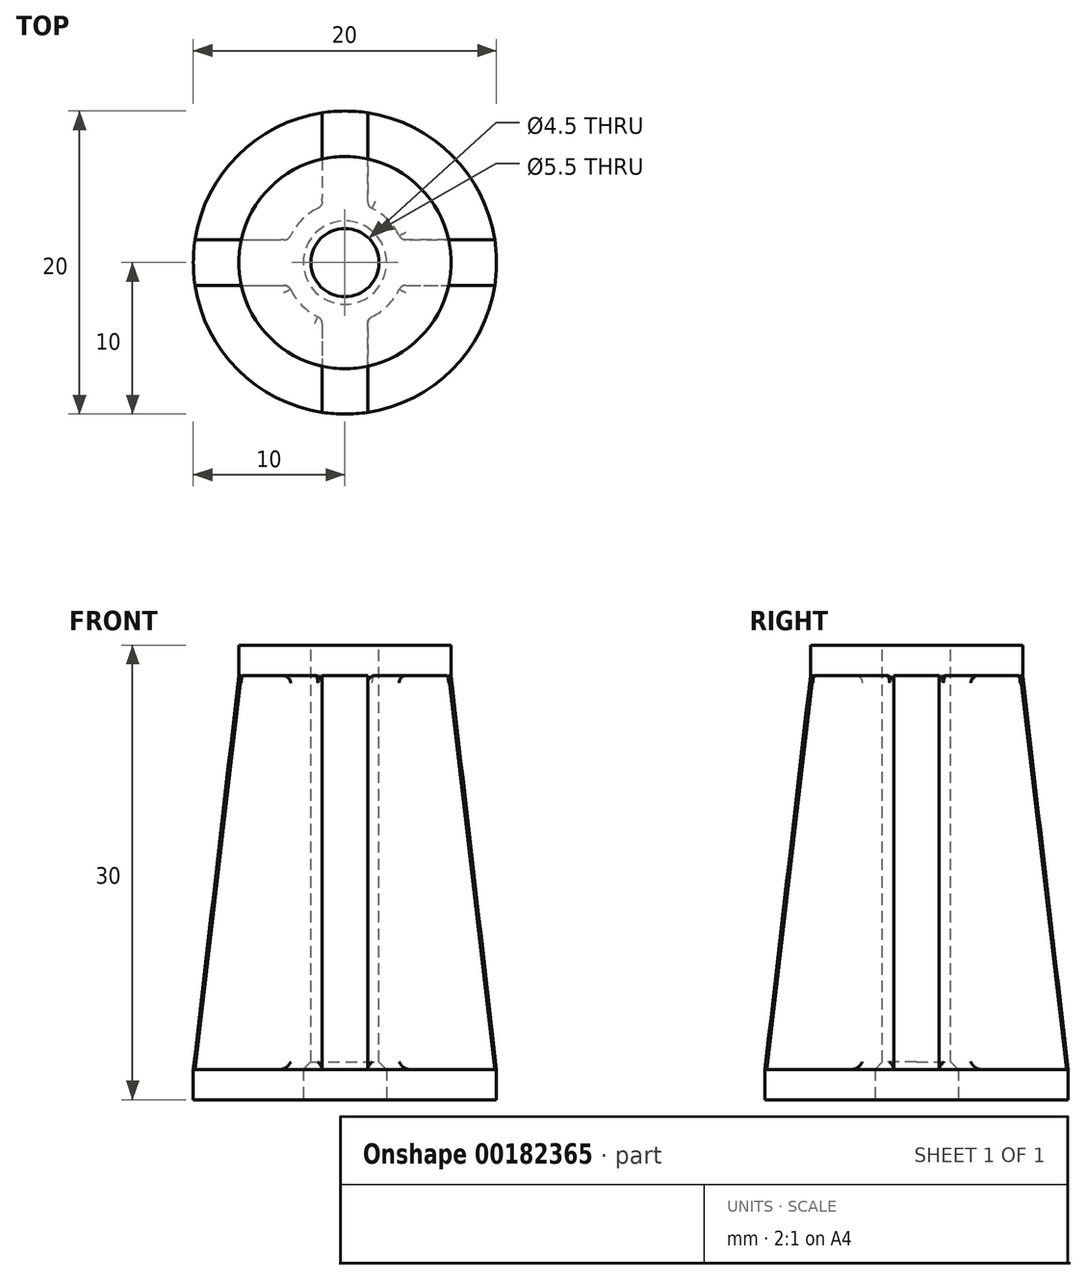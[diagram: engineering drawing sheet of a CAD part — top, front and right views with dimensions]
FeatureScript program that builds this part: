
annotation { "Feature Type Name" : "Feature", "Feature Type Description" : "" }
export const myFeature = defineFeature(function(context is Context, id is Id, definition is map)
    precondition{}
    {
        {
            var Q0;
            Q0=qCreatedBy(makeId("Top.planeOp"),FACE);
            cPlane(context, id + "F0", {"entities" : qUnion([Q0]), "cplaneType" : CPlaneType.OFFSET, "offset" : 28 * mm, "width" : 150 * mm, "height" : 150 * mm});
        }
        {
            var Q0;
            Q0=qCreatedBy(makeId("Top.planeOp"),FACE);
            var sketch = newSketch(context, id + "F1", { "sketchPlane" : qUnion([Q0])});
            skCircle(sketch, "E0", {"center": v(0, 0) * mm, "radius": 10 * mm});
            skSolve(sketch);
        }
        {
            var Q0;
            Q0 = qSketchRegion(id + "F1", true);
            extrude(context, id + "F2", {"entities" : qUnion([Q0]), "depth" : 2 * mm, "offsetDistance" : 25 * mm});
        }
        {
            var Q0;
            Q0=makeQuery(id+"F2.opExtrude","CAP_FACE",FACE,{"disambiguationData":[OSD([sQuery(id+"F1.wireOp",EDGE,"0cac81a4-8bcc-4151-b26c-005e9ad481a4"),sQuery(id+"F1.wireOp",EDGE,"E0")])],"isStart":false});
            var sketch = newSketch(context, id + "F3", { "sketchPlane" : qUnion([Q0])});
            skLineSegment(sketch, "E1", {"start": v(-7.41, 0) * mm, "end": v(8.18, 0) * mm, "construction": true});
            skLineSegment(sketch, "E2", {"start": v(0, 6.98) * mm, "end": v(0, -7.13) * mm, "construction": true});
            skArc(sketch, "E3.0", {"start": v(-1.5, -9.89) * mm, "mid": v(0, -10) * mm, "end": v(1.5, -9.89) * mm});
            skLineSegment(sketch, "E4.0", {"start": v(-9.89, -1.5) * mm, "end": v(-3.7, -1.5) * mm});
            skLineSegment(sketch, "E5.0", {"start": v(-9.89, 1.5) * mm, "end": v(-3.7, 1.5) * mm});
            skLineSegment(sketch, "E6.0", {"start": v(-1.5, 9.89) * mm, "end": v(-1.5, 3.7) * mm});
            skLineSegment(sketch, "E7.0", {"start": v(1.5, 9.89) * mm, "end": v(1.5, 3.7) * mm});
            skArc(sketch, "E8.trimOffspring", {"start": v(9.89, -1.5) * mm, "mid": v(10, 0) * mm, "end": v(9.89, 1.5) * mm});
            skArc(sketch, "E9.trimOffspring", {"start": v(1.5, 9.89) * mm, "mid": v(0, 10) * mm, "end": v(-1.5, 9.89) * mm});
            skArc(sketch, "E10.trimOffspring", {"start": v(-9.89, 1.5) * mm, "mid": v(-10, 0) * mm, "end": v(-9.89, -1.5) * mm});
            skLineSegment(sketch, "E11.trimOffspring", {"start": v(3.7, -1.5) * mm, "end": v(9.89, -1.5) * mm});
            skLineSegment(sketch, "E12.trimOffspring", {"start": v(-1.5, -3.7) * mm, "end": v(-1.5, -9.89) * mm});
            skLineSegment(sketch, "E13.trimOffspring", {"start": v(1.5, -3.7) * mm, "end": v(1.5, -9.89) * mm});
            skArc(sketch, "E14", {"start": v(-3.7, -1.5) * mm, "mid": v(-2.83, -2.83) * mm, "end": v(-1.5, -3.7) * mm});
            skArc(sketch, "E15.trimOffspring", {"start": v(-1.5, 3.7) * mm, "mid": v(-2.83, 2.83) * mm, "end": v(-3.7, 1.5) * mm});
            skLineSegment(sketch, "E16.trimOffspring", {"start": v(3.7, 1.5) * mm, "end": v(9.89, 1.5) * mm});
            skArc(sketch, "E17.trimOffspring", {"start": v(3.7, 1.5) * mm, "mid": v(2.83, 2.83) * mm, "end": v(1.5, 3.7) * mm});
            skArc(sketch, "E18.trimOffspring", {"start": v(1.5, -3.7) * mm, "mid": v(2.83, -2.83) * mm, "end": v(3.7, -1.5) * mm});
            skSolve(sketch);
        }
        {
            var Q0;
            Q0=qCreatedBy(id+"F0.planeOp",FACE);
            var sketch = newSketch(context, id + "F4", { "sketchPlane" : qUnion([Q0])});
            skArc(sketch, "E19", {"start": v(-6.84, 1.5) * mm, "mid": v(-7, 0) * mm, "end": v(-6.84, -1.5) * mm});
            skLineSegment(sketch, "E20.0", {"start": v(1.5, 6.84) * mm, "end": v(1.5, 3.7) * mm});
            skLineSegment(sketch, "E21.0", {"start": v(3.7, 1.5) * mm, "end": v(6.84, 1.5) * mm});
            skLineSegment(sketch, "E22.0", {"start": v(3.7, -1.5) * mm, "end": v(6.84, -1.5) * mm});
            skLineSegment(sketch, "E23.0", {"start": v(1.5, -3.7) * mm, "end": v(1.5, -6.84) * mm});
            skLineSegment(sketch, "E24.0", {"start": v(-1.5, -3.7) * mm, "end": v(-1.5, -6.84) * mm});
            skLineSegment(sketch, "E25.0", {"start": v(-6.84, -1.5) * mm, "end": v(-3.7, -1.5) * mm});
            skLineSegment(sketch, "E26.0", {"start": v(-6.84, 1.5) * mm, "end": v(-3.7, 1.5) * mm});
            skLineSegment(sketch, "E27.0", {"start": v(-1.5, 6.84) * mm, "end": v(-1.5, 3.7) * mm});
            skPoint(sketch, "E28.orphan", {"position": v(1.5, 9.89) * mm});
            skPoint(sketch, "E29.orphan", {"position": v(-1.5, 9.89) * mm});
            skPoint(sketch, "E30.orphan", {"position": v(-9.89, 1.5) * mm});
            skPoint(sketch, "E31.orphan", {"position": v(-9.89, -1.5) * mm});
            skArc(sketch, "E32.trimOffspring", {"start": v(-1.5, -6.84) * mm, "mid": v(0, -7) * mm, "end": v(1.5, -6.84) * mm});
            skArc(sketch, "E33.trimOffspring", {"start": v(6.84, -1.5) * mm, "mid": v(7, 0) * mm, "end": v(6.84, 1.5) * mm});
            skPoint(sketch, "E34.orphan", {"position": v(1.5, -9.89) * mm});
            skPoint(sketch, "E35.orphan", {"position": v(-1.5, -9.89) * mm});
            skPoint(sketch, "E36.orphan", {"position": v(9.89, -1.5) * mm});
            skPoint(sketch, "E37.orphan", {"position": v(5.92, 1.5) * mm});
            skArc(sketch, "E38.trimOffspring", {"start": v(1.5, 6.84) * mm, "mid": v(0, 7) * mm, "end": v(-1.5, 6.84) * mm});
            skArc(sketch, "E39", {"start": v(-3.7, -1.5) * mm, "mid": v(-2.83, -2.83) * mm, "end": v(-1.5, -3.7) * mm});
            skArc(sketch, "E40.trimOffspring", {"start": v(-1.5, 3.7) * mm, "mid": v(-2.83, 2.83) * mm, "end": v(-3.7, 1.5) * mm});
            skArc(sketch, "E41.trimOffspring", {"start": v(1.5, -3.7) * mm, "mid": v(2.83, -2.83) * mm, "end": v(3.7, -1.5) * mm});
            skArc(sketch, "E42.trimOffspring", {"start": v(3.7, 1.5) * mm, "mid": v(2.83, 2.83) * mm, "end": v(1.5, 3.7) * mm});
            skSolve(sketch);
        }
        {
            var Q1;
            Q1 = qSketchRegion(id + "F3", true);
            var Q2;
            Q2 = qSketchRegion(id + "F4", true);
            loft(context, id + "F5", {"operationType" : NewBodyOperationType.ADD, "sheetProfilesArray" : [{ "sheetProfileEntities" : qUnion([Q1]) }, { "sheetProfileEntities" : qUnion([Q2]) }]});
        }
        {
            var Q0;
            Q0=makeQuery(id+"F5.opLoft","CAP_FACE",FACE,{"disambiguationData":[OSD([makeQuery(id+"F4.imprint","IMPRINT",FACE,{"disambiguationData":[TD([[makeQuery(id+"F4.imprint","IMPRINT",EDGE,{"derivedFrom":sQuery(id+"F4.wireOp",EDGE,"E19")}),1.0]])]})])],"isStart":true});
            var sketch = newSketch(context, id + "F6", { "sketchPlane" : qUnion([Q0])});
            skCircle(sketch, "E43", {"center": v(0, 0) * mm, "radius": 7 * mm});
            skSolve(sketch);
        }
        {
            var Q0;
            Q0 = qSketchRegion(id + "F6", true);
            extrude(context, id + "F7", {"entities" : qUnion([Q0]), "operationType" : NewBodyOperationType.ADD, "depth" : 2 * mm, "offsetDistance" : 25 * mm});
        }
        {
            var Q0;
            Q0=makeQuery(id+"F7.opExtrude","CAP_FACE",FACE,{"disambiguationData":[OSD([sQuery(id+"F6.wireOp",EDGE,"E43")])],"isStart":false});
            var sketch = newSketch(context, id + "F8", { "sketchPlane" : qUnion([Q0])});
            skCircle(sketch, "E44", {"center": v(0, 0) * mm, "radius": 2.25 * mm});
            skSolve(sketch);
        }
        {
            var Q0;
            Q0 = qSketchRegion(id + "F8", true);
            extrude(context, id + "F9", {"entities" : qUnion([Q0]), "operationType" : NewBodyOperationType.REMOVE, "endBound" : BoundingType.THROUGH_ALL, "oppositeDirection" : true, "depth" : 25 * mm, "offsetDistance" : 25 * mm});
        }
        {
            var Q0;
            Q0=makeQuery(id+"F5.opLoft","MID_CAP_EDGE",EDGE,{"disambiguationData":[OSD([sQuery(id+"F3.wireOp",EDGE,"E5.0"),sQuery(id+"F3.wireOp",EDGE,"E6.0"),sQuery(id+"F3.wireOp",EDGE,"E15.trimOffspring")])],"capPos":0.0});
            var Q1;
            Q1=makeQuery(id+"F5.opLoft","SWEPT_EDGE",EDGE,{"disambiguationData":[OSD([sQuery(id+"F3.wireOp",EDGE,"E6.0"),sQuery(id+"F3.wireOp",EDGE,"E15.trimOffspring"),sQuery(id+"F4.wireOp",EDGE,"E27.0"),sQuery(id+"F4.wireOp",EDGE,"E40.trimOffspring")])]});
            var Q2;
            Q2=makeQuery(id+"F5.opLoft","SWEPT_FACE",FACE,{"disambiguationData":[OSD([sQuery(id+"F3.wireOp",EDGE,"E5.0"),sQuery(id+"F3.wireOp",EDGE,"E6.0"),sQuery(id+"F3.wireOp",EDGE,"E15.trimOffspring"),sQuery(id+"F4.wireOp",EDGE,"E26.0"),sQuery(id+"F4.wireOp",EDGE,"E27.0"),sQuery(id+"F4.wireOp",EDGE,"E40.trimOffspring")])]});
            var Q3;
            Q3=makeQuery(id+"F5.opLoft","SWEPT_FACE",FACE,{"disambiguationData":[OSD([sQuery(id+"F3.wireOp",EDGE,"E4.0"),sQuery(id+"F3.wireOp",EDGE,"E12.trimOffspring"),sQuery(id+"F3.wireOp",EDGE,"E14"),sQuery(id+"F4.wireOp",EDGE,"E24.0"),sQuery(id+"F4.wireOp",EDGE,"E25.0"),sQuery(id+"F4.wireOp",EDGE,"E39")])]});
            var Q4;
            Q4=makeQuery(id+"F5.opLoft","SWEPT_FACE",FACE,{"disambiguationData":[OSD([sQuery(id+"F3.wireOp",EDGE,"E11.trimOffspring"),sQuery(id+"F3.wireOp",EDGE,"E13.trimOffspring"),sQuery(id+"F3.wireOp",EDGE,"E18.trimOffspring"),sQuery(id+"F4.wireOp",EDGE,"E22.0"),sQuery(id+"F4.wireOp",EDGE,"E23.0"),sQuery(id+"F4.wireOp",EDGE,"E41.trimOffspring")])]});
            var Q5;
            Q5=makeQuery(id+"F5.opLoft","SWEPT_FACE",FACE,{"disambiguationData":[OSD([sQuery(id+"F3.wireOp",EDGE,"E7.0"),sQuery(id+"F3.wireOp",EDGE,"E16.trimOffspring"),sQuery(id+"F3.wireOp",EDGE,"E17.trimOffspring"),sQuery(id+"F4.wireOp",EDGE,"E20.0"),sQuery(id+"F4.wireOp",EDGE,"E21.0"),sQuery(id+"F4.wireOp",EDGE,"E42.trimOffspring")])]});
            var Q6;
            Q6=makeQuery(id+"F5.opLoft","MID_CAP_EDGE",EDGE,{"disambiguationData":[OSD([sQuery(id+"F4.wireOp",EDGE,"E24.0"),sQuery(id+"F4.wireOp",EDGE,"E32.trimOffspring"),sQuery(id+"F4.wireOp",EDGE,"E39")])],"capPos":1.0});
            var Q7;
            Q7=makeQuery(id+"F5.opLoft","MID_CAP_EDGE",EDGE,{"disambiguationData":[OSD([sQuery(id+"F4.wireOp",EDGE,"E19"),sQuery(id+"F4.wireOp",EDGE,"E25.0"),sQuery(id+"F4.wireOp",EDGE,"E39")])],"capPos":1.0});
            var Q8;
            Q8=makeQuery(id+"F5.opLoft","MID_CAP_EDGE",EDGE,{"disambiguationData":[OSD([sQuery(id+"F4.wireOp",EDGE,"E19"),sQuery(id+"F4.wireOp",EDGE,"E26.0"),sQuery(id+"F4.wireOp",EDGE,"E40.trimOffspring")])],"capPos":1.0});
            var Q9;
            Q9=makeQuery(id+"F5.opLoft","MID_CAP_EDGE",EDGE,{"disambiguationData":[OSD([sQuery(id+"F4.wireOp",EDGE,"E27.0"),sQuery(id+"F4.wireOp",EDGE,"E38.trimOffspring"),sQuery(id+"F4.wireOp",EDGE,"E40.trimOffspring")])],"capPos":1.0});
            var Q10;
            Q10=makeQuery(id+"F5.opLoft","MID_CAP_EDGE",EDGE,{"disambiguationData":[OSD([sQuery(id+"F4.wireOp",EDGE,"E20.0"),sQuery(id+"F4.wireOp",EDGE,"E38.trimOffspring"),sQuery(id+"F4.wireOp",EDGE,"E42.trimOffspring")])],"capPos":1.0});
            var Q11;
            Q11=makeQuery(id+"F5.opLoft","MID_CAP_EDGE",EDGE,{"disambiguationData":[OSD([sQuery(id+"F4.wireOp",EDGE,"E21.0"),sQuery(id+"F4.wireOp",EDGE,"E33.trimOffspring"),sQuery(id+"F4.wireOp",EDGE,"E42.trimOffspring")])],"capPos":1.0});
            var Q12;
            Q12=makeQuery(id+"F5.opLoft","MID_CAP_EDGE",EDGE,{"disambiguationData":[OSD([sQuery(id+"F4.wireOp",EDGE,"E22.0"),sQuery(id+"F4.wireOp",EDGE,"E33.trimOffspring"),sQuery(id+"F4.wireOp",EDGE,"E41.trimOffspring")])],"capPos":1.0});
            var Q13;
            Q13=makeQuery(id+"F5.opLoft","MID_CAP_EDGE",EDGE,{"disambiguationData":[OSD([sQuery(id+"F4.wireOp",EDGE,"E23.0"),sQuery(id+"F4.wireOp",EDGE,"E32.trimOffspring"),sQuery(id+"F4.wireOp",EDGE,"E41.trimOffspring")])],"capPos":1.0});
            fillet(context, id + "F10", {"entities" : qUnion([Q0, Q1, Q2, Q3, Q4, Q5, Q6, Q7, Q8, Q9, Q10, Q11, Q12, Q13]), "radius" : 0.5 * mm, "tangentPropagation" : true, "allowEdgeOverflow" : false});
        }
        {
            var Q0;
            Q0=makeQuery(id+"F2.opExtrude","CAP_FACE",FACE,{"disambiguationData":[OSD([sQuery(id+"F1.wireOp",EDGE,"E0")])],"isStart":true});
            var sketch = newSketch(context, id + "F11", { "sketchPlane" : qUnion([Q0])});
            skCircle(sketch, "E45", {"center": v(0, 0) * mm, "radius": 2.75 * mm});
            skSolve(sketch);
        }
        {
            var Q0;
            Q0 = qSketchRegion(id + "F11", true);
            extrude(context, id + "F12", {"entities" : qUnion([Q0]), "operationType" : NewBodyOperationType.REMOVE, "oppositeDirection" : true, "depth" : 2.5 * mm, "offsetDistance" : 25 * mm});
        }
        {
            var Q0;
            Q0=makeQuery(id+"F12.boolean.opBoolean","COPY",EDGE,{"derivedFrom":makeQuery(id+"F12.opExtrude","CAP_EDGE",EDGE,{"disambiguationData":[OSD([sQuery(id+"F11.wireOp",EDGE,"E45")])],"isStart":false})});
            var Q1;
            Q1=makeQuery(id+"F12.boolean.opBoolean","COPY",EDGE,{"derivedFrom":makeQuery(id+"F12.opExtrude","CAP_EDGE",EDGE,{"disambiguationData":[OSD([sQuery(id+"F11.wireOp",EDGE,"E45")])],"isStart":true})});
            chamfer(context, id + "F13", {"entities" : qUnion([Q0, Q1]), "width" : 0.5 * mm, "tangentPropagation" : true});
        }
    });
